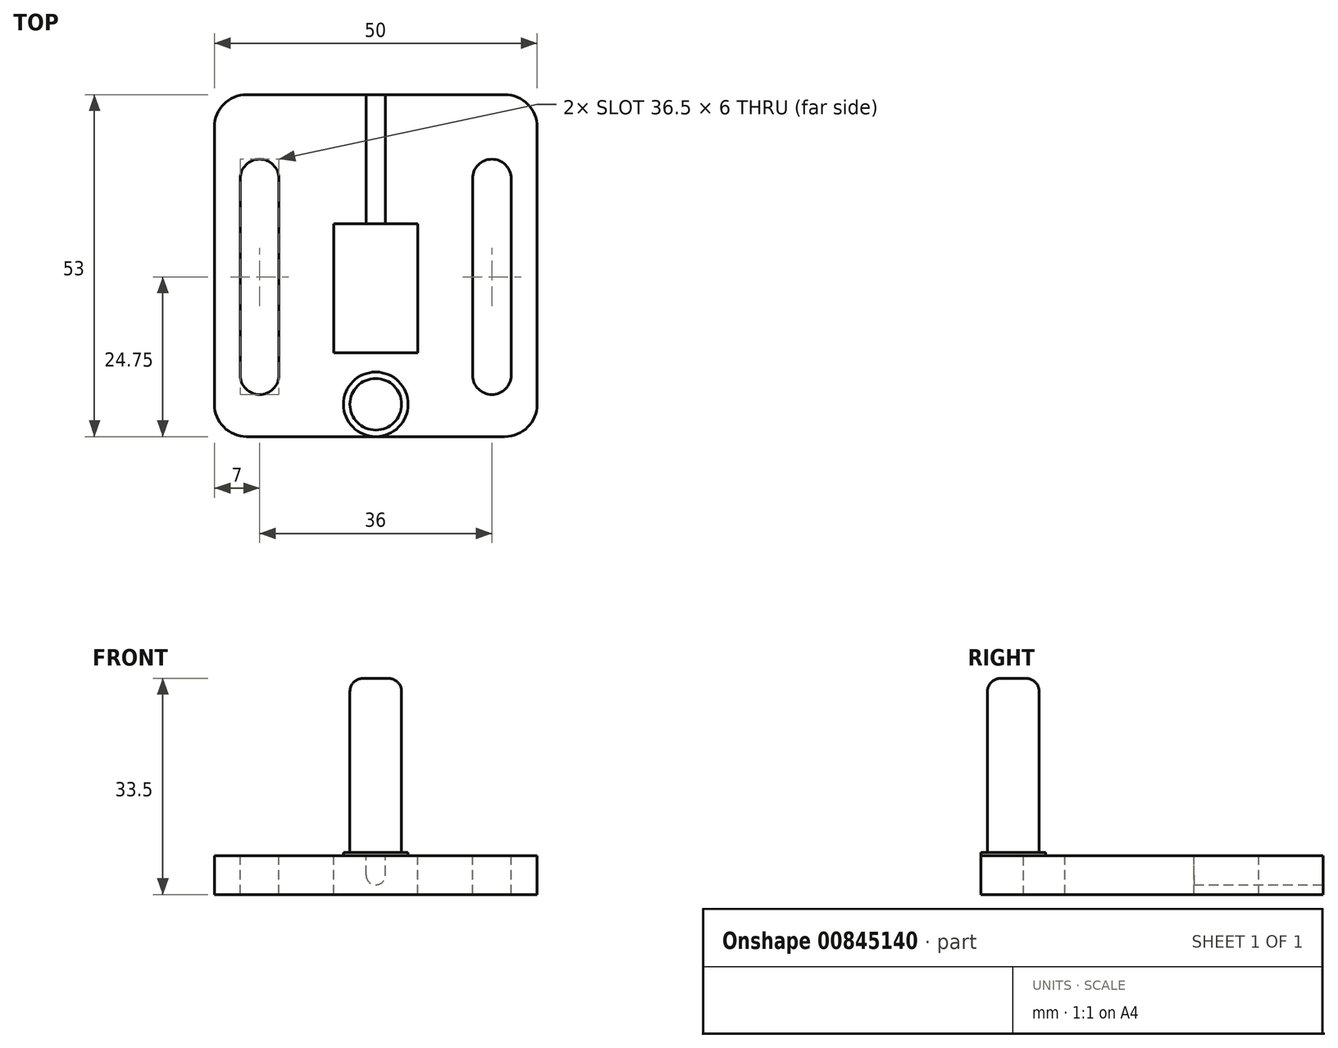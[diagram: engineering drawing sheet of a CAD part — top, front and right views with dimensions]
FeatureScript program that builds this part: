
annotation { "Feature Type Name" : "Feature", "Feature Type Description" : "" }
export const myFeature = defineFeature(function(context is Context, id is Id, definition is map)
    precondition{}
    {
        {
            var Q0;
            Q0=qCreatedBy(makeId("Top.planeOp"),FACE);
            var sketch = newSketch(context, id + "F0", { "sketchPlane" : qUnion([Q0])});
            skLineSegment(sketch, "E0.bottom", {"start": v(25, 25) * mm, "end": v(-25, 25) * mm, "construction": true});
            skLineSegment(sketch, "E0.top", {"start": v(25, -25) * mm, "end": v(-25, -25) * mm, "construction": true});
            skLineSegment(sketch, "E0.left", {"start": v(25, 25) * mm, "end": v(25, -25) * mm, "construction": true});
            skLineSegment(sketch, "E0.right", {"start": v(-25, 25) * mm, "end": v(-25, -25) * mm, "construction": true});
            skPoint(sketch, "E0.middle", {"position": v(0, 0) * mm});
            skCircle(sketch, "E1", {"center": v(0, 0) * mm, "radius": 19 * mm, "construction": true});
            skCircle(sketch, "E2", {"center": v(0, 0) * mm, "radius": 15 * mm, "construction": true});
            skCircle(sketch, "E3", {"center": v(0, 27) * mm, "radius": 12 * mm, "construction": true});
            skLineSegment(sketch, "E4", {"start": v(-25, 75) * mm, "end": v(25, 75) * mm});
            skLineSegment(sketch, "E5", {"start": v(25, 75) * mm, "end": v(25, 22) * mm});
            skLineSegment(sketch, "E6", {"start": v(25, 22) * mm, "end": v(-25, 22) * mm});
            skCircle(sketch, "E7", {"center": v(0, 27) * mm, "radius": 4 * mm});
            skCircle(sketch, "E8", {"center": v(0, 27) * mm, "radius": 5 * mm});
            skLineSegment(sketch, "E9", {"start": v(-25, 75) * mm, "end": v(-25, 22) * mm});
            skLineSegment(sketch, "E10.bottom", {"start": v(-25, 25) * mm, "end": v(25, 25) * mm, "construction": true});
            skLineSegment(sketch, "E10.top", {"start": v(-25, 75) * mm, "end": v(25, 75) * mm, "construction": true});
            skLineSegment(sketch, "E10.left", {"start": v(-25, 25) * mm, "end": v(-25, 75) * mm, "construction": true});
            skLineSegment(sketch, "E10.right", {"start": v(25, 25) * mm, "end": v(25, 75) * mm, "construction": true});
            skLineSegment(sketch, "E11.bottom", {"start": v(-6.5, 55) * mm, "end": v(6.5, 55) * mm, "construction": true});
            skLineSegment(sketch, "E11.top", {"start": v(-6.5, 46.5) * mm, "end": v(6.5, 46.5) * mm, "construction": true});
            skLineSegment(sketch, "E11.left", {"start": v(-6.5, 55) * mm, "end": v(-6.5, 46.5) * mm, "construction": true});
            skLineSegment(sketch, "E11.right", {"start": v(6.5, 55) * mm, "end": v(6.5, 46.5) * mm, "construction": true});
            skLineSegment(sketch, "E12", {"start": v(-15, 55) * mm, "end": v(-6.5, 55) * mm, "construction": true});
            skLineSegment(sketch, "E13.bottom", {"start": v(-21, 65) * mm, "end": v(-15, 65) * mm});
            skLineSegment(sketch, "E13.top", {"start": v(-21, 25) * mm, "end": v(-15, 25) * mm});
            skLineSegment(sketch, "E13.left", {"start": v(-21, 65) * mm, "end": v(-21, 25) * mm});
            skLineSegment(sketch, "E13.right", {"start": v(-15, 65) * mm, "end": v(-15, 25) * mm});
            skLineSegment(sketch, "E14.bottom", {"start": v(-6.5, 55) * mm, "end": v(6.5, 55) * mm});
            skLineSegment(sketch, "E14.top", {"start": v(-6.5, 35) * mm, "end": v(6.5, 35) * mm});
            skLineSegment(sketch, "E14.left", {"start": v(-6.5, 55) * mm, "end": v(-6.5, 35) * mm});
            skLineSegment(sketch, "E14.right", {"start": v(6.5, 55) * mm, "end": v(6.5, 35) * mm});
            skLineSegment(sketch, "E15.top", {"start": v(15, 25) * mm, "end": v(21, 25) * mm});
            skLineSegment(sketch, "E15.left", {"start": v(15, 65) * mm, "end": v(15, 25) * mm});
            skLineSegment(sketch, "E15.right", {"start": v(21, 65) * mm, "end": v(21, 25) * mm});
            skLineSegment(sketch, "E16", {"start": v(21, 65) * mm, "end": v(15, 65) * mm});
            skLineSegment(sketch, "E17", {"start": v(-15, 28.5) * mm, "end": v(-21, 28.5) * mm});
            skLineSegment(sketch, "E18", {"start": v(21, 28.5) * mm, "end": v(15, 28.5) * mm});
            skSolve(sketch);
        }
        {
            var Q0;
            Q0=qSketchRegion(id+"F0",true);
            var Q1;
            Q1=makeQuery(id+"F0.imprint","IMPRINT",FACE,{"disambiguationData":[TD([[makeQuery(id+"F0.imprint","IMPRINT",EDGE,{"derivedFrom":sQuery(id+"F0.wireOp",EDGE,"E7")}),1.0]])]});
            var Q2;
            Q2=makeQuery(id+"F0.imprint","IMPRINT",FACE,{"disambiguationData":[TD([[makeQuery(id+"F0.imprint","IMPRINT",EDGE,{"derivedFrom":sQuery(id+"F0.wireOp",EDGE,"E7")}),-1.0]])]});
            var Q3;
            {var subQ0=sQuery(id+"F0.wireOp",EDGE,"E15.top");Q3=makeQuery(id+"F0.imprint","IMPRINT",FACE,{"disambiguationData":[TD([[makeQuery(id+"F0.imprint","IMPRINT",EDGE,{"derivedFrom":subQ0}),1.0]])]});}
            var Q4;
            {var subQ0=sQuery(id+"F0.wireOp",EDGE,"E13.top");Q4=makeQuery(id+"F0.imprint","IMPRINT",FACE,{"disambiguationData":[TD([[makeQuery(id+"F0.imprint","IMPRINT",EDGE,{"derivedFrom":subQ0}),1.0]])]});}
            extrude(context, id + "F1", {"entities" : qUnion([Q0, Q1, Q2, Q3, Q4]), "oppositeDirection" : true, "depth" : 6 * mm, "offsetDistance" : 25 * mm});
        }
        {
            var Q0;
            Q0=makeQuery(id+"F0.imprint","IMPRINT",FACE,{"disambiguationData":[TD([[makeQuery(id+"F0.imprint","IMPRINT",EDGE,{"derivedFrom":sQuery(id+"F0.wireOp",EDGE,"E7")}),1.0]])]});
            var Q1;
            Q1=makeQuery(id+"F0.imprint","IMPRINT",FACE,{"disambiguationData":[TD([[makeQuery(id+"F0.imprint","IMPRINT",EDGE,{"derivedFrom":sQuery(id+"F0.wireOp",EDGE,"E7")}),-1.0]])]});
            extrude(context, id + "F2", {"entities" : qUnion([Q0, Q1]), "operationType" : NewBodyOperationType.ADD, "depth" : 0.5 * mm, "offsetDistance" : 25 * mm});
        }
        {
            var Q0;
            Q0=makeQuery(id+"F2.opExtrude","CAP_FACE",FACE,{"disambiguationData":[OSD([sQuery(id+"F0.wireOp",EDGE,"E8")])],"isStart":false});
            var sketch = newSketch(context, id + "F3", { "sketchPlane" : qUnion([Q0])});
            skCircle(sketch, "E19", {"center": v(0, 27) * mm, "radius": 4 * mm});
            skSolve(sketch);
        }
        {
            var Q0;
            Q0=qSketchRegion(id+"F3",true);
            extrude(context, id + "F4", {"entities" : qUnion([Q0]), "operationType" : NewBodyOperationType.ADD, "depth" : 27 * mm, "offsetDistance" : 25 * mm});
        }
        {
            var Q0;
            Q0=makeQuery(id+"F4.opExtrude","CAP_FACE",FACE,{"disambiguationData":[OSD([sQuery(id+"F3.wireOp",EDGE,"E19")])],"isStart":false});
            fillet(context, id + "F5", {"entities" : qUnion([Q0]), "radius" : 2 * mm, "tangentPropagation" : true, "allowEdgeOverflow" : false});
        }
        {
            var Q0;
            Q0=makeQuery(id+"F1.opExtrude","SWEPT_FACE",FACE,{"disambiguationData":[OSD([sQuery(id+"F0.wireOp",EDGE,"E4")])]});
            var sketch = newSketch(context, id + "F6", { "sketchPlane" : qUnion([Q0])});
            skLineSegment(sketch, "E20", {"start": v(-25, -3) * mm, "end": v(25, -3) * mm, "construction": true});
            skLineSegment(sketch, "E21", {"start": v(0, 0) * mm, "end": v(0, -6) * mm, "construction": true});
            skCircle(sketch, "E22", {"center": v(0, -3) * mm, "radius": 1.5 * mm});
            skLineSegment(sketch, "E23", {"start": v(-1.5, -3) * mm, "end": v(-1.5, 0) * mm});
            skLineSegment(sketch, "E24", {"start": v(1.5, -3) * mm, "end": v(1.5, 0) * mm});
            skLineSegment(sketch, "E25", {"start": v(1.5, 0) * mm, "end": v(-1.5, 0) * mm});
            skSolve(sketch);
        }
        {
            var Q0;
            Q0 = qSketchRegion(id + "F6", true);
            extrude(context, id + "F7", {"entities" : qUnion([Q0]), "operationType" : NewBodyOperationType.REMOVE, "endBound" : BoundingType.UP_TO_NEXT, "oppositeDirection" : true, "depth" : 25 * mm, "offsetDistance" : 25 * mm});
        }
        {
            var Q0;
            Q0=makeQuery(id+"F1.opExtrude","SWEPT_EDGE",EDGE,{"disambiguationData":[OSD([sQuery(id+"F0.wireOp",EDGE,"E4"),sQuery(id+"F0.wireOp",EDGE,"E5")])]});
            var Q1;
            Q1=makeQuery(id+"F1.opExtrude","SWEPT_EDGE",EDGE,{"disambiguationData":[OSD([sQuery(id+"F0.wireOp",EDGE,"E4"),sQuery(id+"F0.wireOp",EDGE,"E9")])]});
            var Q2;
            Q2=makeQuery(id+"F1.opExtrude","SWEPT_EDGE",EDGE,{"disambiguationData":[OSD([sQuery(id+"F0.wireOp",EDGE,"E6"),sQuery(id+"F0.wireOp",EDGE,"E9")])]});
            var Q3;
            Q3=makeQuery(id+"F1.opExtrude","SWEPT_EDGE",EDGE,{"disambiguationData":[OSD([sQuery(id+"F0.wireOp",EDGE,"E5"),sQuery(id+"F0.wireOp",EDGE,"E6")])]});
            fillet(context, id + "F8", {"entities" : qUnion([Q0, Q1, Q2, Q3]), "radius" : 5 * mm, "tangentPropagation" : true, "allowEdgeOverflow" : false});
        }
        {
            var Q0;
            Q0=makeQuery(id+"F1.opExtrude","SWEPT_EDGE",EDGE,{"disambiguationData":[OSD([sQuery(id+"F0.wireOp",EDGE,"E13.top"),sQuery(id+"F0.wireOp",EDGE,"E13.right")])]});
            var Q1;
            Q1=makeQuery(id+"F1.opExtrude","SWEPT_EDGE",EDGE,{"disambiguationData":[OSD([sQuery(id+"F0.wireOp",EDGE,"E13.top"),sQuery(id+"F0.wireOp",EDGE,"E13.left")])]});
            var Q2;
            Q2=makeQuery(id+"F1.opExtrude","SWEPT_EDGE",EDGE,{"disambiguationData":[OSD([sQuery(id+"F0.wireOp",EDGE,"E15.top"),sQuery(id+"F0.wireOp",EDGE,"E15.right")])]});
            var Q3;
            Q3=makeQuery(id+"F1.opExtrude","SWEPT_EDGE",EDGE,{"disambiguationData":[OSD([sQuery(id+"F0.wireOp",EDGE,"E15.top"),sQuery(id+"F0.wireOp",EDGE,"E15.left")])]});
            var Q4;
            Q4=makeQuery(id+"F1.opExtrude","SWEPT_EDGE",EDGE,{"disambiguationData":[OSD([sQuery(id+"F0.wireOp",EDGE,"E15.right"),sQuery(id+"F0.wireOp",EDGE,"E16")])]});
            var Q5;
            Q5=makeQuery(id+"F1.opExtrude","SWEPT_EDGE",EDGE,{"disambiguationData":[OSD([sQuery(id+"F0.wireOp",EDGE,"E13.bottom"),sQuery(id+"F0.wireOp",EDGE,"E13.right")])]});
            var Q6;
            Q6=makeQuery(id+"F1.opExtrude","SWEPT_EDGE",EDGE,{"disambiguationData":[OSD([sQuery(id+"F0.wireOp",EDGE,"E13.bottom"),sQuery(id+"F0.wireOp",EDGE,"E13.left")])]});
            var Q7;
            Q7=makeQuery(id+"F1.opExtrude","SWEPT_EDGE",EDGE,{"disambiguationData":[OSD([sQuery(id+"F0.wireOp",EDGE,"E15.left"),sQuery(id+"F0.wireOp",EDGE,"E16")])]});
            fillet(context, id + "F9", {"entities" : qUnion([Q0, Q1, Q2, Q3, Q4, Q5, Q6, Q7]), "radius" : 3 * mm, "tangentPropagation" : true, "allowEdgeOverflow" : false});
        }
    });
